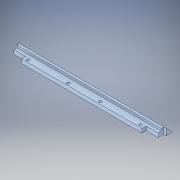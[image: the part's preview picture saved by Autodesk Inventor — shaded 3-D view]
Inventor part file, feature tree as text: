
AUTODESK INVENTOR PART (.ipt)
format: ipt  version: 2019 (Build 230136000, 136)  size: 218,624 bytes
history: native  units: mm
features: sketch x6, extrude x5, direct_edit x1, hole x1, fillet x1, move_body x1
ambient origin geometry x8: Origin, YZ Plane, XZ Plane, XY Plane, X Axis, Y Axis, Z Axis, Center Point
bodies: Solid2 (feature_tree), Solid1 (feature_tree)
feature tree (15):
  extrude  "Extrusion1"  Depth=1.0mm
  extrude  "Extrusion2"  Depth=186.0mm TaperAngle=0.0deg
  extrude  "Extrusion3"  Depth=5.8mm
  extrude  "Extrusion4"  Depth=5.8mm
  extrude  "Extrusion5"  Depth=1.0mm TaperAngle=0.0deg
  direct_edit  "Direct Edit1"
  hole  "Hole1"  [1 undecoded]
  fillet  "Fillet1"  Radius=186.0mm
  sketch  "Sketch1"  dims[d0=186.0mm d1=1.0mm]
  sketch  "Sketch2"  dims[d2=1.0mm d3=0.0mm d4=186.0mm d5=0.0mm]
  sketch  "Sketch3"  dims[d6=186.0mm d7=0.0mm d9=5.8mm]
  sketch  "Sketch4"  dims[d10=5.8mm d11=5.8mm]
  sketch  "Sketch5"  dims[d12=5.8mm d13=1.0mm d14=0.0mm]
  sketch  "Sketch6"  dims[d15=1.9mm d16=1.9mm d17=186.0mm d18=0.0mm d19=0.0mm d20=0.0mm d21=3.0mm d22=3.0mm d23=5.0mm d24=50.0mm d25=40.0mm d26=50.0mm d27=3.4mm d28=6.0mm d29=6.9mm d30=2.0mm d31=15.7mm d32=8.0mm d33=20.594885mm d34=1.0mm]
  move_body  "Move1"
note: 1 required parameter value undecoded (feature->parameter linkage not recoverable at this tier; creation-order binding heuristic only, values carry confidence <= 0.55)
